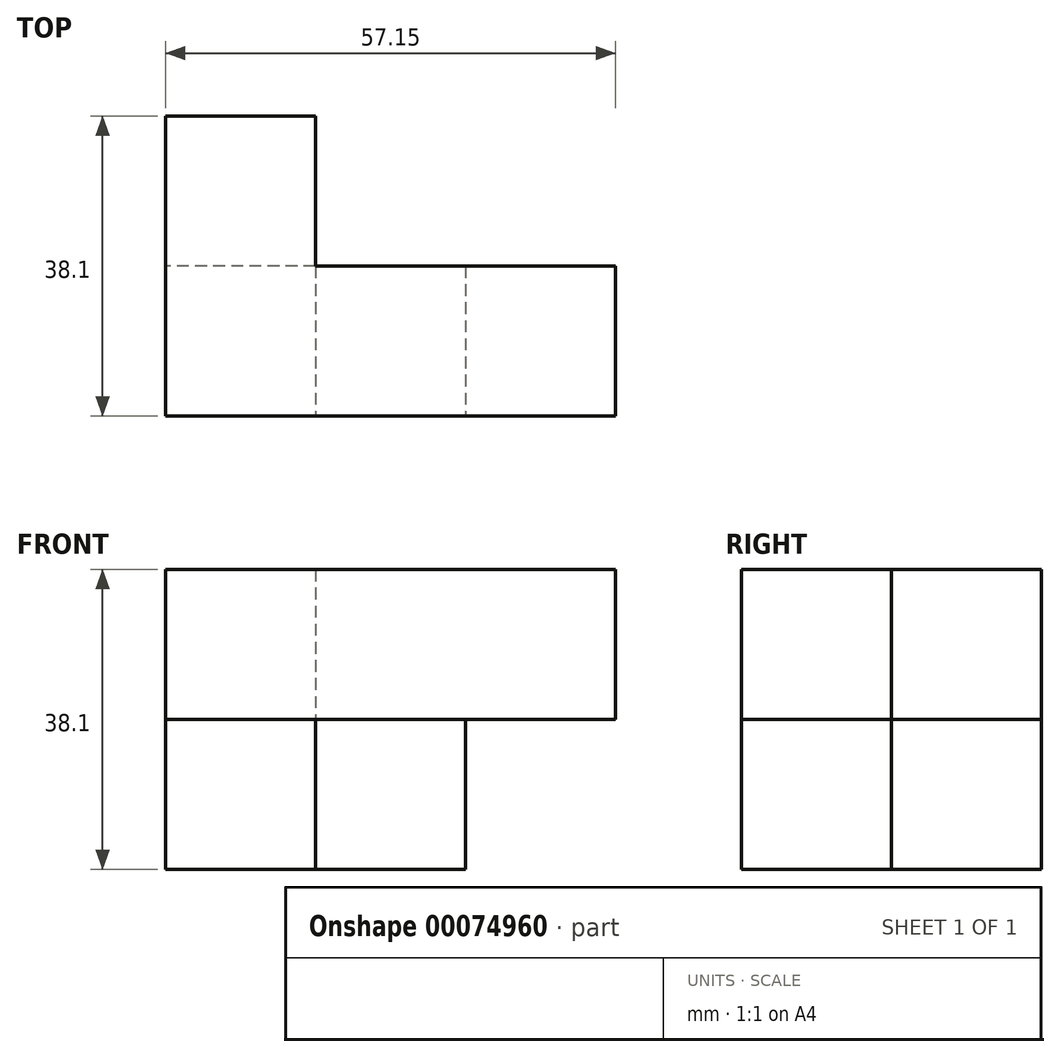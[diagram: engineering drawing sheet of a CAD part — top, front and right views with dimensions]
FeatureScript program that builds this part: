
annotation { "Feature Type Name" : "Feature", "Feature Type Description" : "" }
export const myFeature = defineFeature(function(context is Context, id is Id, definition is map)
    precondition{}
    {
        {
            var Q0;
            Q0=qCreatedBy(makeId("Top.planeOp"),FACE);
            var sketch = newSketch(context, id + "F0", { "sketchPlane" : qUnion([Q0])});
            skLineSegment(sketch, "E0", {"start": v(0, 0) * mm, "end": v(57.15, 0) * mm});
            skLineSegment(sketch, "E1", {"start": v(57.15, 0) * mm, "end": v(57.15, 19.05) * mm});
            skLineSegment(sketch, "E2", {"start": v(57.15, 19.05) * mm, "end": v(19.05, 19.05) * mm});
            skLineSegment(sketch, "E3", {"start": v(19.05, 19.05) * mm, "end": v(19.05, 38.1) * mm});
            skLineSegment(sketch, "E4", {"start": v(19.05, 38.1) * mm, "end": v(0, 38.1) * mm});
            skLineSegment(sketch, "E5", {"start": v(0, 38.1) * mm, "end": v(0, 0) * mm});
            skSolve(sketch);
        }
        {
            var Q0;
            Q0 = qSketchRegion(id + "F0", true);
            extrude(context, id + "F1", {"entities" : qUnion([Q0]), "depth" : 19.05 * mm});
        }
        {
            var Q0;
            Q0=makeQuery(id+"F1.opExtrude","CAP_FACE",FACE,{"disambiguationData":[OSD([sQuery(id+"F0.wireOp",EDGE,"E0"),sQuery(id+"F0.wireOp",EDGE,"E1"),sQuery(id+"F0.wireOp",EDGE,"E2"),sQuery(id+"F0.wireOp",EDGE,"E3"),sQuery(id+"F0.wireOp",EDGE,"E4"),sQuery(id+"F0.wireOp",EDGE,"E5")])],"isStart":true});
            var sketch = newSketch(context, id + "F2", { "sketchPlane" : qUnion([Q0])});
            skLineSegment(sketch, "E6.bottom", {"start": v(19.05, -19.05) * mm, "end": v(0, -19.05) * mm});
            skLineSegment(sketch, "E6.top", {"start": v(19.05, -38.1) * mm, "end": v(0, -38.1) * mm});
            skLineSegment(sketch, "E6.left", {"start": v(19.05, -19.05) * mm, "end": v(19.05, -38.1) * mm});
            skLineSegment(sketch, "E6.right", {"start": v(0, -19.05) * mm, "end": v(0, -38.1) * mm});
            skLineSegment(sketch, "E7.bottom", {"start": v(19.05, -19.05) * mm, "end": v(38.1, -19.05) * mm});
            skLineSegment(sketch, "E7.top", {"start": v(19.05, 0) * mm, "end": v(38.1, 0) * mm});
            skLineSegment(sketch, "E7.left", {"start": v(19.05, -19.05) * mm, "end": v(19.05, 0) * mm});
            skLineSegment(sketch, "E7.right", {"start": v(38.1, -19.05) * mm, "end": v(38.1, 0) * mm});
            skSolve(sketch);
        }
        {
            var Q0;
            Q0 = qSketchRegion(id + "F2", true);
            extrude(context, id + "F3", {"entities" : qUnion([Q0]), "depth" : 19.05 * mm});
        }
    });
